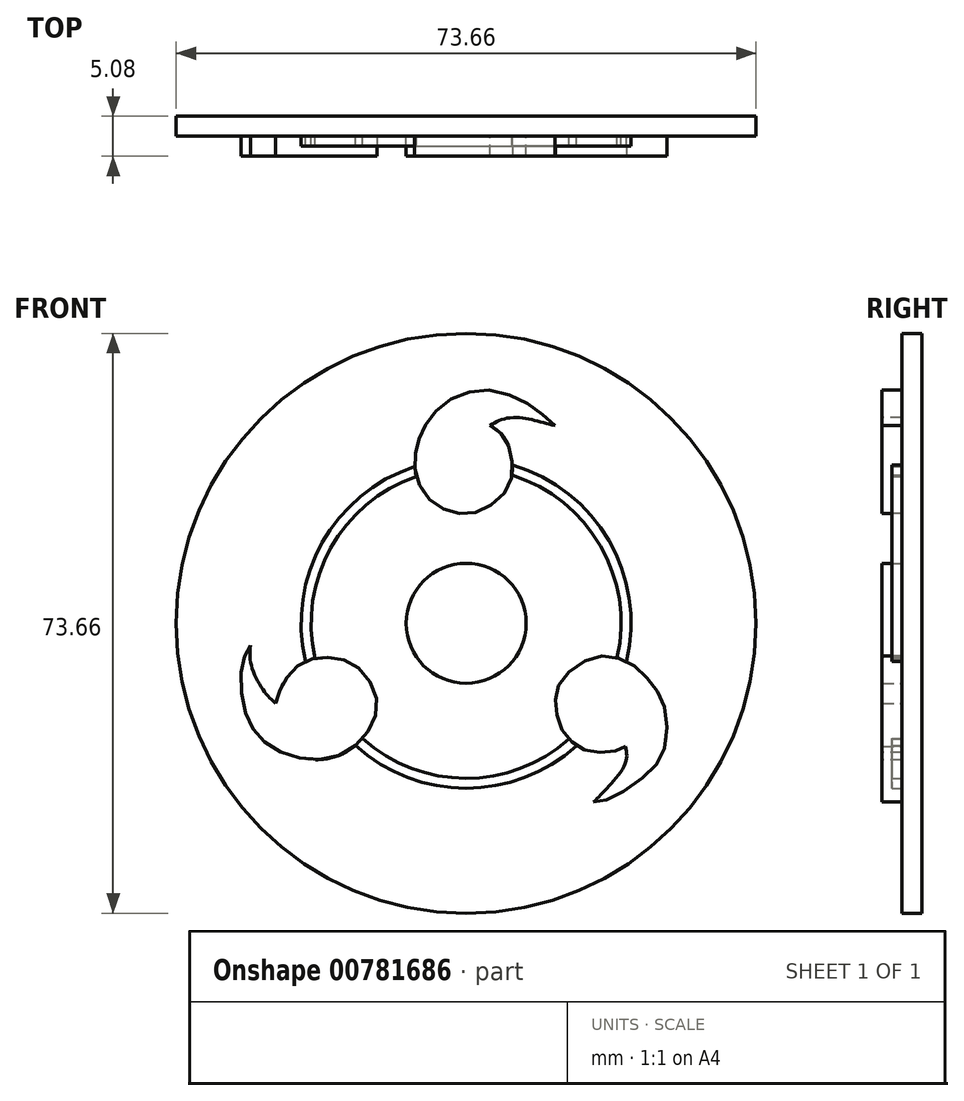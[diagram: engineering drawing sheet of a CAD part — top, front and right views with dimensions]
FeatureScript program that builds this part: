
annotation { "Feature Type Name" : "Feature", "Feature Type Description" : "" }
export const myFeature = defineFeature(function(context is Context, id is Id, definition is map)
    precondition{}
    {
        {
            var Q0;
            Q0=qCreatedBy(makeId("Front.planeOp"),FACE);
            var sketch = newSketch(context, id + "F0", { "sketchPlane" : qUnion([Q0])});
            skCircle(sketch, "E0", {"center": v(0, 0) * mm, "radius": 36.83 * mm});
            skSolve(sketch);
        }
        {
            var Q0;
            Q0=qCreatedBy(makeId("Front.planeOp"),FACE);
            var sketch = newSketch(context, id + "F1", { "sketchPlane" : qUnion([Q0])});
            skCircle(sketch, "E1", {"center": v(0, 0) * mm, "radius": 7.62 * mm});
            skSolve(sketch);
        }
        {
            var Q0;
            Q0=qCreatedBy(makeId("Front.planeOp"),FACE);
            var sketch = newSketch(context, id + "F2", { "sketchPlane" : qUnion([Q0])});
            skCircle(sketch, "E2", {"center": v(0, 0) * mm, "radius": 20.96 * mm});
            skCircle(sketch, "E3", {"center": v(0, 0) * mm, "radius": 19.69 * mm});
            skSolve(sketch);
        }
        {
            var Q0;
            Q0=qSketchRegion(id+"F2",true);
            extrude(context, id + "F3", {"entities" : qUnion([Q0]), "depth" : 3.8 * mm});
        }
        {
            var Q0;
            Q0=qSketchRegion(id+"F0",true);
            extrude(context, id + "F4", {"entities" : qUnion([Q0]), "operationType" : NewBodyOperationType.ADD, "depth" : 2.54 * mm});
        }
        {
            var Q0;
            Q0=qSketchRegion(id+"F1",true);
            extrude(context, id + "F5", {"entities" : qUnion([Q0]), "operationType" : NewBodyOperationType.ADD, "depth" : 5.08 * mm});
        }
        {
            var Q0;
            Q0=qCreatedBy(makeId("Front.planeOp"),FACE);
            var sketch = newSketch(context, id + "F6", { "sketchPlane" : qUnion([Q0])});
            skFitSpline(sketch, "E4", {"points": [v(20.26, -15.67) * mm, v(19, -16.23) * mm, v(15.99, -16.33) * mm, v(13.64, -15.25) * mm, v(11.95, -13.04) * mm, v(11.34, -10.23) * mm, v(11.81, -7.79) * mm, v(14.53, -5.07) * mm, v(18.15, -4.18) * mm, v(21.29, -5.4) * mm, v(23.73, -7.88) * mm, v(25.28, -10.98) * mm, v(25.14, -16.05) * mm, v(22.98, -19.14) * mm, v(18.29, -22.29) * mm, v(16.18, -22.7) * mm], "startDerivative": vector(-24.78, -14.45) * mm, "endDerivative": vector(-34.66, -2.02) * mm});
            skFitSpline(sketch, "E5", {"points": [v(20.26, -15.67) * mm, v(20.26, -17.69) * mm, v(17.96, -20.88) * mm, v(16.18, -22.7) * mm], "startDerivative": vector(1.33, -6.74) * mm, "endDerivative": vector(-5.12, -5.1) * mm});
            skFitSpline(sketch, "E6", {"points": [v(3.05, 25.14) * mm, v(4.88, 23.55) * mm, v(5.86, 20.36) * mm, v(5.11, 16.93) * mm, v(1.92, 14.35) * mm, v(-1.5, 14.07) * mm, v(-4.74, 15.85) * mm, v(-6.48, 19.28) * mm, v(-6.24, 22.42) * mm, v(-5.11, 25.33) * mm, v(-1.92, 28.47) * mm, v(3.05, 29.6) * mm, v(8.16, 27.68) * mm, v(11.26, 25.1) * mm], "startDerivative": vector(32.58, -21.63) * mm, "endDerivative": vector(35.17, -33.59) * mm});
            skFitSpline(sketch, "E7", {"points": [v(11.26, 25.1) * mm, v(9.15, 25.66) * mm, v(6.8, 26.13) * mm, v(4.55, 25.9) * mm, v(3.05, 25.14) * mm], "startDerivative": vector(-8.21, 2.2) * mm, "endDerivative": vector(-6.28, -3.82) * mm});
            skFitSpline(sketch, "E8", {"points": [v(-23.92, -10.35) * mm, v(-24.72, -9.71) * mm, v(-26.06, -8.06) * mm, v(-27.34, -5.12) * mm, v(-27.4, -2.83) * mm], "startDerivative": vector(-4.4, 3.18) * mm, "endDerivative": vector(0.68, 8.42) * mm});
            skFitSpline(sketch, "E9", {"points": [v(-27.4, -2.83) * mm, v(-28.4, -5.02) * mm, v(-28.2, -10.73) * mm, v(-26.16, -14.57) * mm, v(-21.62, -17.03) * mm, v(-16.07, -16.76) * mm, v(-12.23, -13.4) * mm, v(-11.42, -9.4) * mm, v(-13.77, -5.6) * mm, v(-17.35, -4.32) * mm, v(-20.88, -5.07) * mm, v(-23.17, -7.52) * mm, v(-24.18, -10.17) * mm], "startDerivative": vector(-18.88, -28.65) * mm, "endDerivative": vector(-11.45, -38.62) * mm});
            skSolve(sketch);
        }
        {
            var Q0;
            Q0=qSketchRegion(id+"F6",true);
            extrude(context, id + "F7", {"entities" : qUnion([Q0]), "operationType" : NewBodyOperationType.ADD, "depth" : 5.08 * mm});
        }
    });
